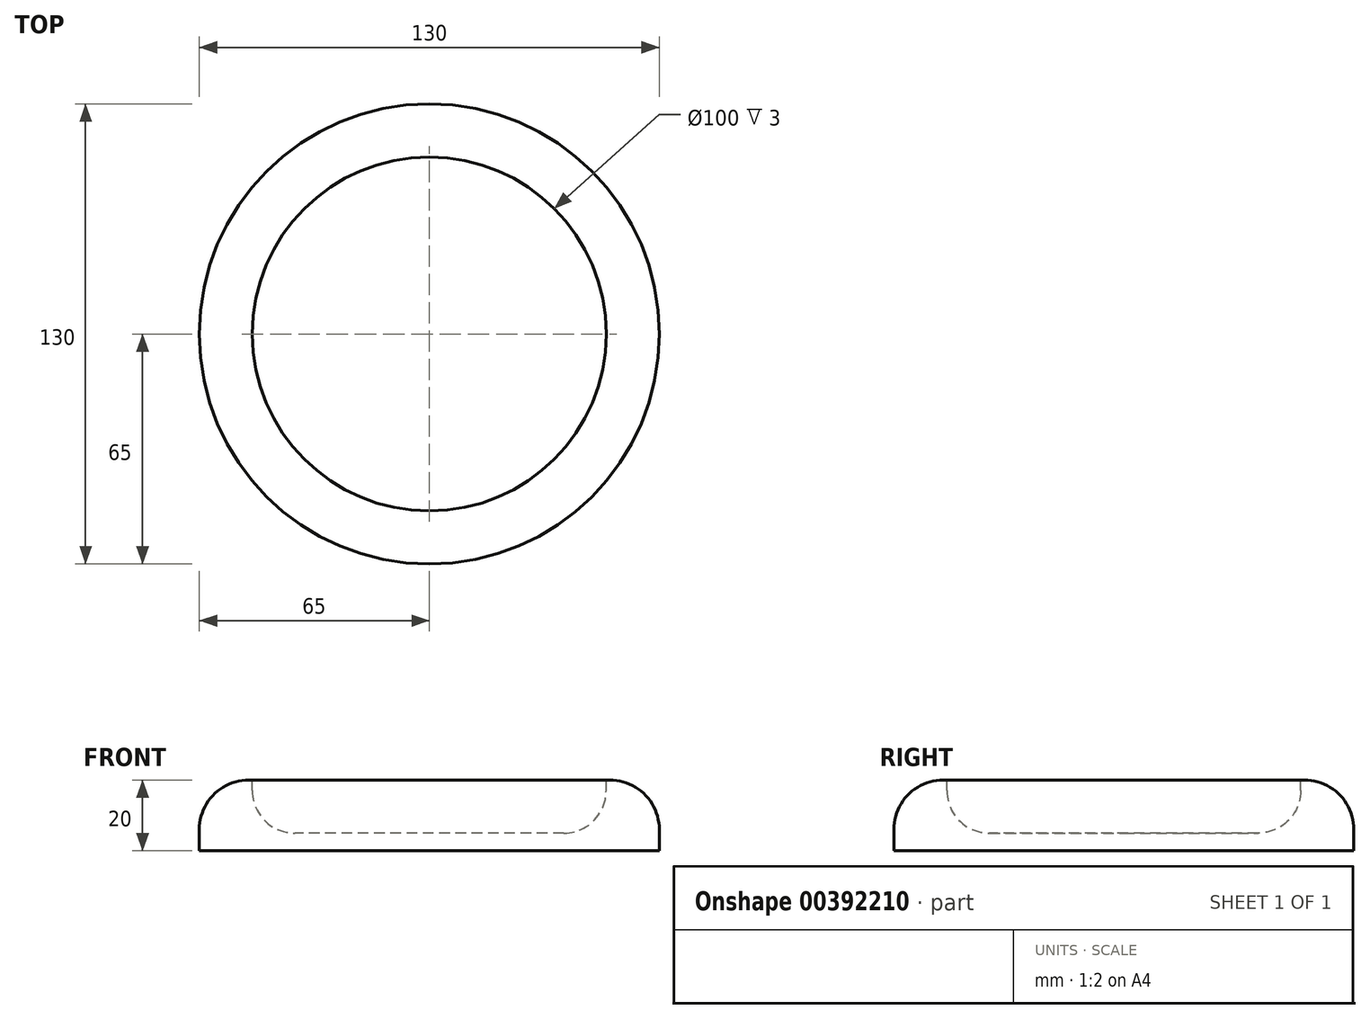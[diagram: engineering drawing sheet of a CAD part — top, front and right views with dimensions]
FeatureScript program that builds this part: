
annotation { "Feature Type Name" : "Feature", "Feature Type Description" : "" }
export const myFeature = defineFeature(function(context is Context, id is Id, definition is map)
    precondition{}
    {
        {
            var Q0;
            Q0=qCreatedBy(makeId("Top.planeOp"),FACE);
            var sketch = newSketch(context, id + "F0", { "sketchPlane" : qUnion([Q0])});
            skCircle(sketch, "E0", {"center": v(0, 0) * mm, "radius": 65 * mm});
            skSolve(sketch);
        }
        {
            var Q0;
            Q0 = qSketchRegion(id + "F0", true);
            extrude(context, id + "F1", {"entities" : qUnion([Q0]), "depth" : 20 * mm});
        }
        {
            var Q0;
            Q0=makeQuery(id+"F1.opExtrude","CAP_FACE",FACE,{"disambiguationData":[OSD([sQuery(id+"F0.wireOp",EDGE,"E0")])],"isStart":false});
            var sketch = newSketch(context, id + "F2", { "sketchPlane" : qUnion([Q0])});
            skCircle(sketch, "E1", {"center": v(0, 0) * mm, "radius": 50 * mm});
            skSolve(sketch);
        }
        {
            var Q0;
            Q0 = qSketchRegion(id + "F2", true);
            extrude(context, id + "F3", {"entities" : qUnion([Q0]), "operationType" : NewBodyOperationType.REMOVE, "oppositeDirection" : true, "depth" : 15 * mm});
        }
        {
            var Q0;
            Q0=makeQuery(id+"F1.opExtrude","CAP_EDGE",EDGE,{"disambiguationData":[OSD([sQuery(id+"F0.wireOp",EDGE,"E0")])],"isStart":false});
            fillet(context, id + "F4", {"entities" : qUnion([Q0]), "radius" : 14 * mm, "tangentPropagation" : true, "allowEdgeOverflow" : false});
        }
        {
            var Q0;
            Q0=makeQuery(id+"F3.boolean.opBoolean","COPY",EDGE,{"derivedFrom":makeQuery(id+"F3.opExtrude","CAP_EDGE",EDGE,{"disambiguationData":[OSD([sQuery(id+"F2.wireOp",EDGE,"E1")])],"isStart":false})});
            fillet(context, id + "F5", {"entities" : qUnion([Q0]), "radius" : 12 * mm, "tangentPropagation" : true, "allowEdgeOverflow" : false});
        }
        {
            var Q0;
            Q0=qCreatedBy(makeId("Front.planeOp"),FACE);
            cPlane(context, id + "F6", {"entities" : qUnion([Q0]), "cplaneType" : CPlaneType.OFFSET, "offset" : 65 * mm, "width" : 150 * mm, "height" : 150 * mm});
        }
    });
